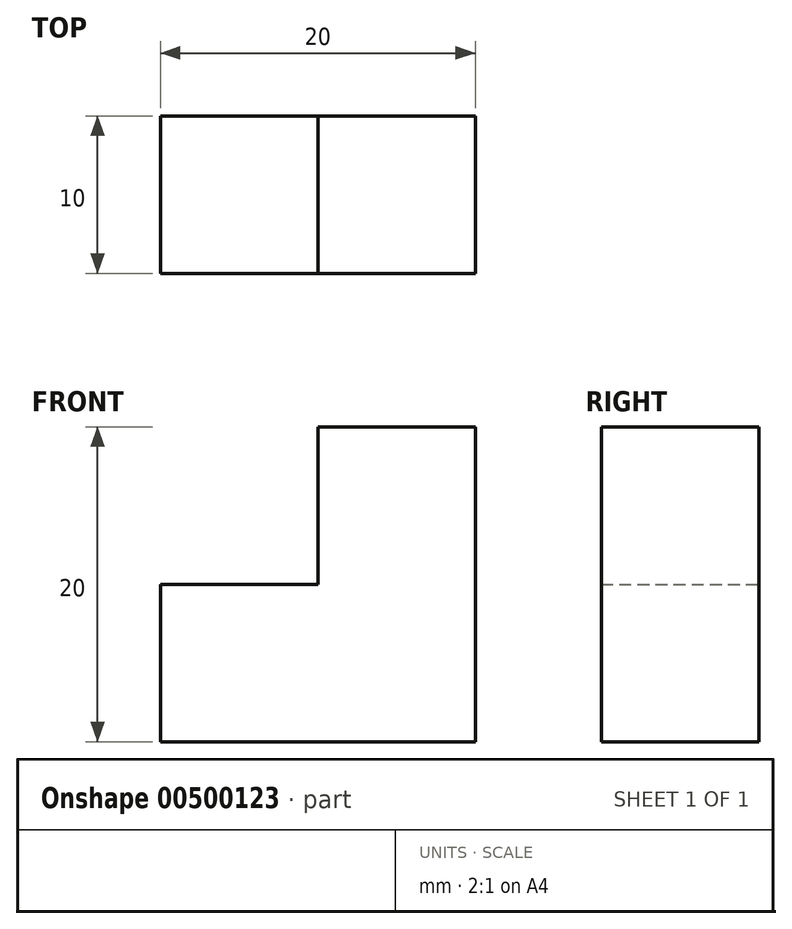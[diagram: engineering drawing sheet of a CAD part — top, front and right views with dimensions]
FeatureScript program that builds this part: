
annotation { "Feature Type Name" : "Feature", "Feature Type Description" : "" }
export const myFeature = defineFeature(function(context is Context, id is Id, definition is map)
    precondition{}
    {
        {
            var Q0;
            Q0=qCreatedBy(makeId("Front.planeOp"),FACE);
            var sketch = newSketch(context, id + "F0", { "sketchPlane" : qUnion([Q0])});
            skLineSegment(sketch, "E0", {"start": v(0, 0) * mm, "end": v(-10, 0) * mm});
            skLineSegment(sketch, "E1", {"start": v(-10, 0) * mm, "end": v(-10, -10) * mm});
            skLineSegment(sketch, "E2", {"start": v(-10, -10) * mm, "end": v(10, -10) * mm});
            skLineSegment(sketch, "E3", {"start": v(10, -10) * mm, "end": v(10, 10) * mm});
            skLineSegment(sketch, "E4", {"start": v(10, 10) * mm, "end": v(0, 10) * mm});
            skLineSegment(sketch, "E5", {"start": v(0, 10) * mm, "end": v(0, 0) * mm});
            skSolve(sketch);
        }
        {
            var Q0;
            Q0=makeQuery(id+"F0.imprint","IMPRINT",FACE,{"disambiguationData":[TD([[makeQuery(id+"F0.imprint","IMPRINT",EDGE,{"derivedFrom":sQuery(id+"F0.wireOp",EDGE,"E0")}),1.0]])]});
            extrude(context, id + "F1", {"entities" : qUnion([Q0]), "depth" : 10 * mm});
        }
    });
